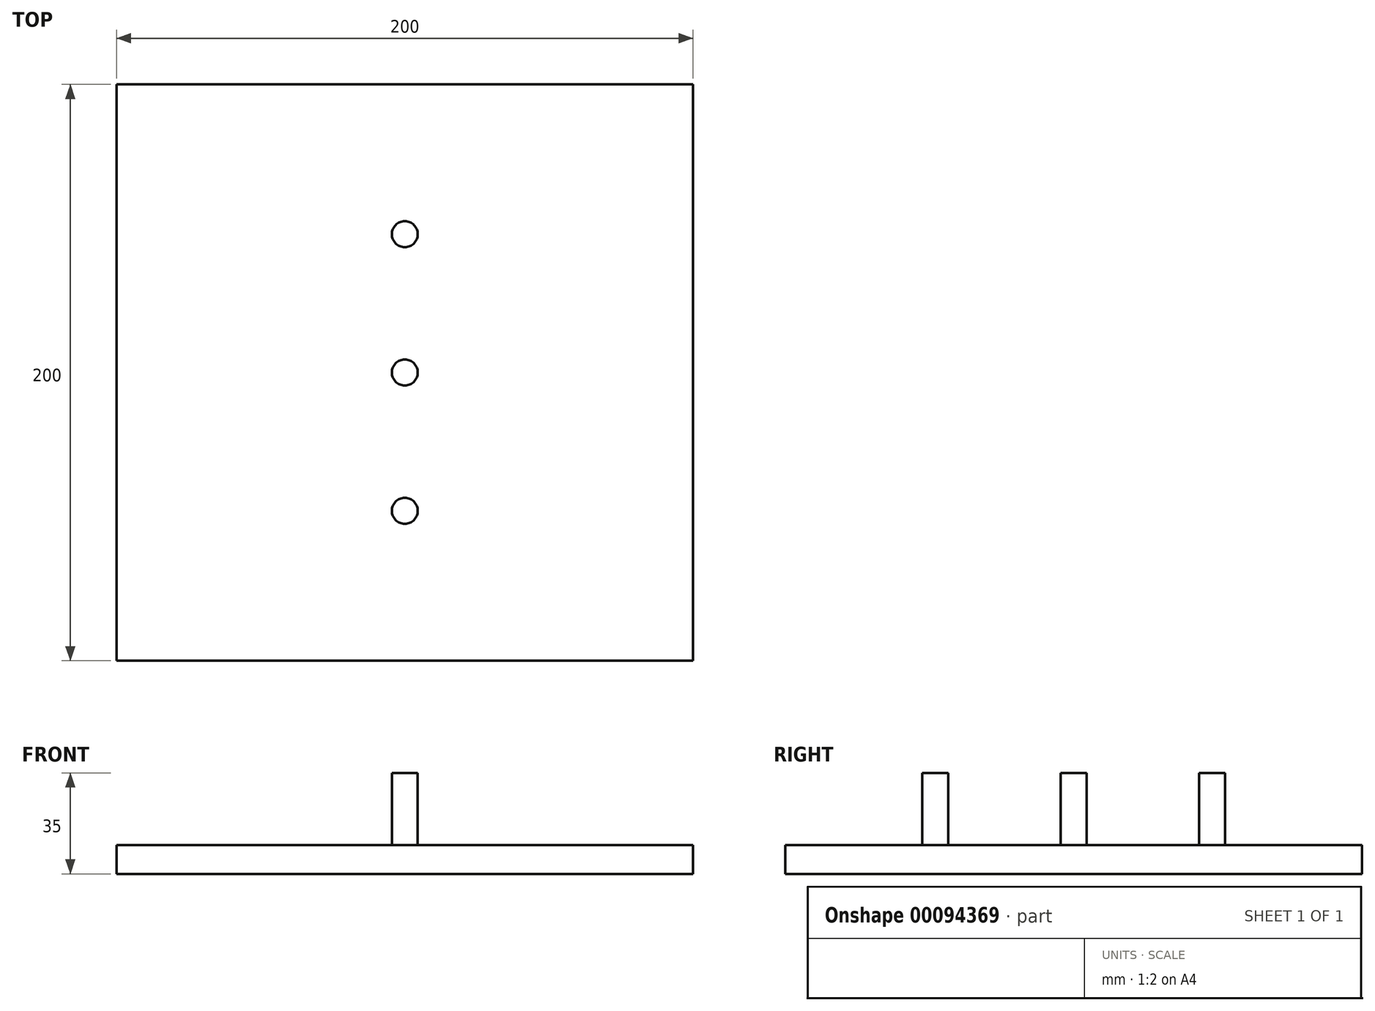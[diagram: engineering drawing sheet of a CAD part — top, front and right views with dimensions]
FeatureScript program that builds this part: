
annotation { "Feature Type Name" : "Feature", "Feature Type Description" : "" }
export const myFeature = defineFeature(function(context is Context, id is Id, definition is map)
    precondition{}
    {
        {
            var Q0;
            Q0=qCreatedBy(makeId("Top.planeOp"),FACE);
            var sketch = newSketch(context, id + "F0", { "sketchPlane" : qUnion([Q0])});
            skLineSegment(sketch, "E0.bottom", {"start": v(100, 100) * mm, "end": v(-100, 100) * mm});
            skLineSegment(sketch, "E0.top", {"start": v(100, -100) * mm, "end": v(-100, -100) * mm});
            skLineSegment(sketch, "E0.left", {"start": v(100, 100) * mm, "end": v(100, -100) * mm});
            skLineSegment(sketch, "E0.right", {"start": v(-100, 100) * mm, "end": v(-100, -100) * mm});
            skPoint(sketch, "E0.middle", {"position": v(0, 0) * mm});
            skLineSegment(sketch, "E1", {"start": v(0, 100) * mm, "end": v(0, -100) * mm, "construction": true});
            skLineSegment(sketch, "E2", {"start": v(-100, 0) * mm, "end": v(100, 0) * mm, "construction": true});
            skLineSegment(sketch, "E3", {"start": v(-100, 45) * mm, "end": v(100, 45) * mm, "construction": true});
            skLineSegment(sketch, "E4", {"start": v(-100, -45) * mm, "end": v(100, -45) * mm, "construction": true});
            skSolve(sketch);
        }
        {
            var Q0;
            Q0=makeQuery(id+"F0.imprint","IMPRINT",FACE,{"disambiguationData":[TD([[makeQuery(id+"F0.imprint","IMPRINT",EDGE,{"derivedFrom":sQuery(id+"F0.wireOp",EDGE,"E0.bottom")}),1.0]])]});
            extrude(context, id + "F1", {"entities" : qUnion([Q0]), "depth" : 10 * mm});
        }
        {
            var Q0;
            Q0=makeQuery(id+"F1.opExtrude","CAP_FACE",FACE,{"disambiguationData":[OSD([sQuery(id+"F0.wireOp",EDGE,"E0.bottom"),sQuery(id+"F0.wireOp",EDGE,"E0.top"),sQuery(id+"F0.wireOp",EDGE,"E0.left"),sQuery(id+"F0.wireOp",EDGE,"E0.right")])],"isStart":false});
            var sketch = newSketch(context, id + "F2", { "sketchPlane" : qUnion([Q0])});
            skLineSegment(sketch, "E5", {"start": v(-100, 0) * mm, "end": v(100, 0) * mm, "construction": true});
            skLineSegment(sketch, "E6", {"start": v(0, 100) * mm, "end": v(0, -100) * mm, "construction": true});
            skLineSegment(sketch, "E7", {"start": v(-100, 48) * mm, "end": v(100, 48) * mm, "construction": true});
            skLineSegment(sketch, "E8", {"start": v(-100, -48) * mm, "end": v(100, -48) * mm, "construction": true});
            skCircle(sketch, "E9", {"center": v(0, 48) * mm, "radius": 4.5 * mm});
            skCircle(sketch, "E10.MirrorC", {"center": v(0, -48) * mm, "radius": 4.5 * mm});
            skLineSegment(sketch, "E11", {"start": v(-100, -24) * mm, "end": v(100, -24) * mm, "construction": true});
            skCircle(sketch, "E12.MirrorC", {"center": v(0, 0) * mm, "radius": 4.5 * mm});
            skSolve(sketch);
        }
        {
            var Q0;
            Q0 = qSketchRegion(id + "F2", true);
            extrude(context, id + "F3", {"entities" : qUnion([Q0]), "operationType" : NewBodyOperationType.ADD, "depth" : 25 * mm});
        }
    });
